# Revit family: 05-1507-21-M1
name_source: partatom
category: Luminarias
revit_build: Autodesk Revit 2017 (Build: 20160225_1515(x64)
units: mm (PartAtom-declared; Revit-internal decimal feet)

## family parameters
Compartido = Sí
Corte con vacíos al cargar = No
Cota de conector redondo = Diámetro de uso
Número OmniClass = 23.80.70.00
Origen de luz = No
Punto de cálculo de habitación = No
Se basa en plano de trabajo = No
Siempre vertical = Sí
Tipo de pieza = Normal
Título OmniClass = Lighting

## types (1)
- 05-1507-21-M1
    Acabado = Cromo, Opal
    CRI = 80
    Catálogo = Decorative
    CodigoGubimclass = 50.60.50.20
    CodigoOmniclass = 21-04 50 40
    CodigoUniclass2015 = EF_70_80
    CodigoUniformat2010 = D5040
    DescripcionGubimclass = Iluminación interior
    DescripcionOmniclass = Lighting
    DescripcionUniclass2015 = Lighting
    DescripcionUniformat2010 = Lighting
    EAN13 = 8435381452704
    Eficiencia energética = LED A++
    Etiqueta V/f = 100-240V/50-60Hz
    Fabricante = LEDS C4
    Familia = Toilet Q 580mm
    FechaVersion = Julio 2020
    Ficha = http://files.leds-c4.com
    Fotometría = http://files.leds-c4.com
    Fuente de luz = 60xLED 8 700.00 lm
    IMC = http://files.leds-c4.com
    IP = IP44
    IfcExportAs = IfcLightFixture
    IfcExportType = NOTDEFINED
    Imagen web = http://files.leds-c4.com
    LDT = http://files.leds-c4.com
    Lumenes reales (lm) = 367
    Material = Aluminio, Policarbonato
    Peso neto (KG) = 0.76
    Pluma comercial = http://files.leds-c4.com
    Producto descatalogado = Catalogado ES
    Referencia = 05-1507-21-M1
    Temperatura color led (K) = Blanco cálido - 3000K
    Tender text (Castellano) = LEDS C4
Toilet Q 580mm
05-1507-21-M1V1

Aplique de uso interior para iluminar frontalmente. 

Diseño atemporal. Protección IP ideal para el baño. Alta durabilidad para uso intensivo. Material estructura: Aluminio. Acabado estructura: Cromo. Material difusor: Policarbonato. Acabado difusor: Opal. Garantía: 5 Años.

Peso neto del producto (Kg): 0.760
Anchura o diámetro del producto (mm): 580
Altura del producto (mm): 40
Salida del producto (mm): 75

Clase 2. Prueba hilo incandescente: 850. IP: IP44. LED. Nº de portalámparas o Leds: 60. Marca del LED: REFOND. Marca del Driver: HGPOWER. Potencia máxima de la fuente de luz: 8W. Temperatura de color: Blanco cálido - 3000K. Índice de reproducción cromática: 80. Steps Mac Adam: 3. Diámetro máximo de la bombilla que admite la luminaria: 50.000h L80B20. UGR:  10.0. Riesgo fotobiológico: RG0. Flujo real (lm): 367. Flujo nominal (lm): 700. Lm/W reales: 31. Voltaje: 24. Equipo incluido: Si, electrónico. Equipo multivoltaje incluido. Potencia total: 11.7. Factor de potencia: 0.50.
    Tender text (English) = LEDS C4
Toilet Q 580mm
05-1507-21-M1V1

Wall light for indoor use. 

For frontal lighting. Timeless design. IP protection, ideal for bathrooms. High durability for intensive use. Structure material: Aluminium. Structure finish: Chrome. Diffuser material: Polycarbonate. Diffuser finish: Opal. Warranty: 5 Years.

Product net weight (Kg): 0.760
Product width or diameter (mm): 580
Product height (mm): 40
Product aperture (mm): 75

Class 2. Glow wire test: 850. IP: IP44. LED. No. of lampholders or LEDs: 60. LED brand: REFOND. Driver brand: HGPOWER. Maximum power of light source: 8W. Colour temperature: LED warm-white 3000K. Colour rendering index: 80. MacAdam Steps: 3. Maximum diameter of luminaire bulb: 50.000h L80B20. UGR:  10.0. Photobiological risk: RG0. Real flux (lm): 367. Nominal flux (lm): 700. Lm/Real W: 31. Voltage: 24. Gear included: Yes, electronic. Multi-voltage gear included. Total power: 11.7. Power factor: 0.50.
    Tipo = Baño
    Vatios (W) = 11.7
    Versión = v1
